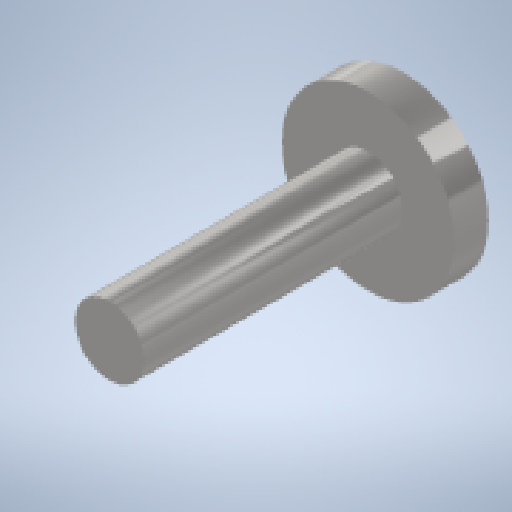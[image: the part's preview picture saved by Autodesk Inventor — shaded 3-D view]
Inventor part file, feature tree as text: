
AUTODESK INVENTOR PART (.ipt)
format: ipt  version: 2024 (Build 280153000, 153)  size: 138,752 bytes
history: native  units: mm
features: extrude x2, sketch x2, other x1
ambient origin geometry x8: Origin, YZ Plane, XZ Plane, XY Plane, X Axis, Y Axis, Z Axis, Center Point
bodies: Body1 (feature_tree)
feature tree (5):
  other  "솔리드1"
  extrude  "돌출1"  Depth=4.0mm
  extrude  "돌출2"  Depth=15.0mm TaperAngle=0.0deg
  sketch  "스케치1"
  sketch  "스케치2"
